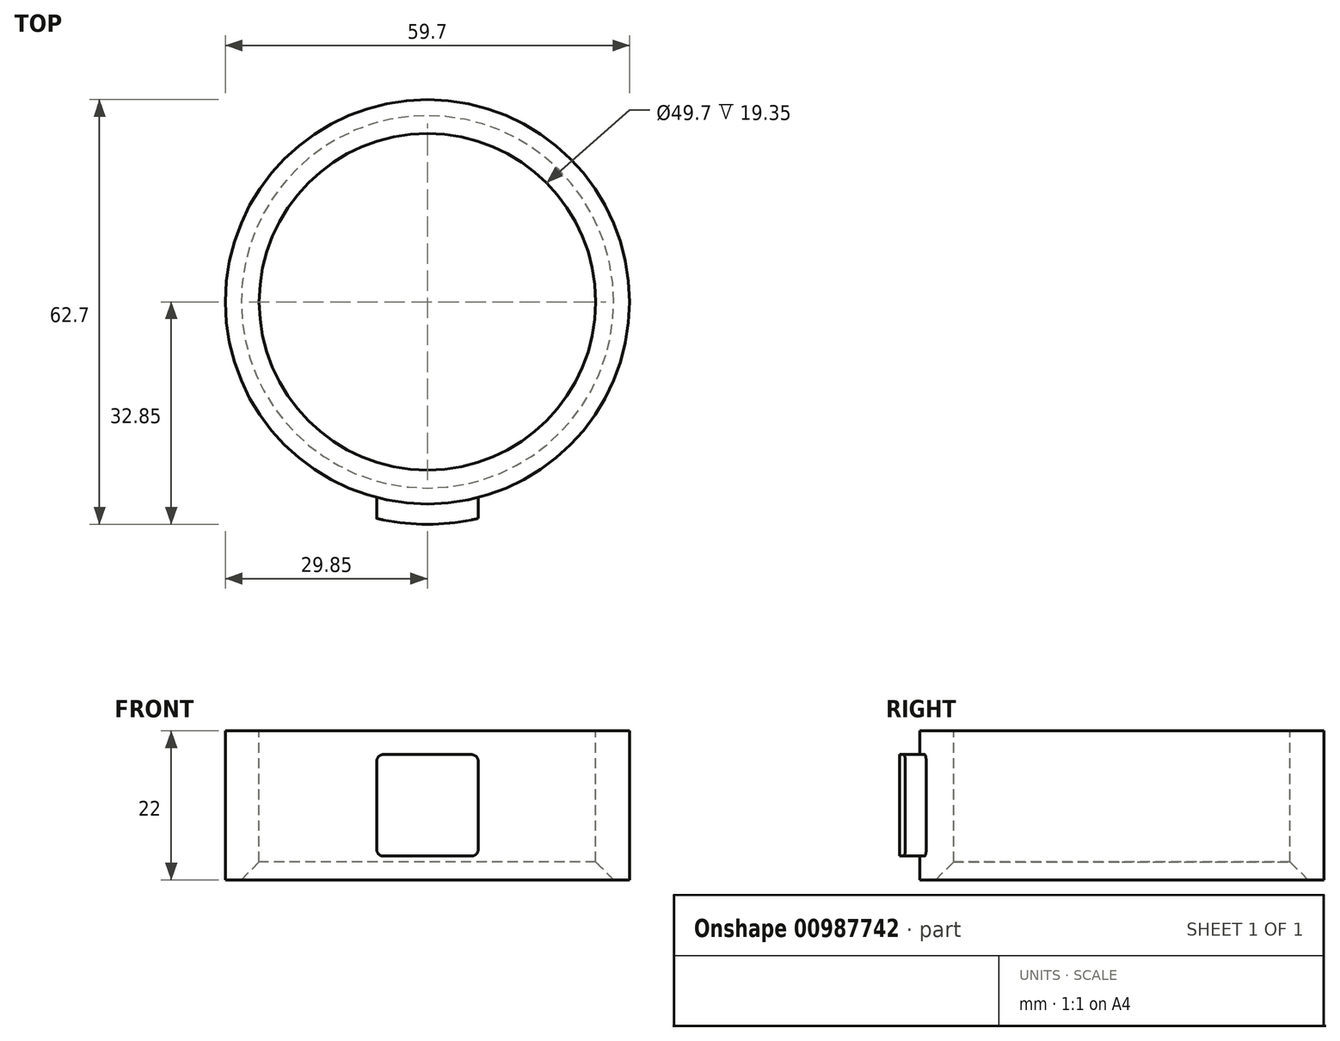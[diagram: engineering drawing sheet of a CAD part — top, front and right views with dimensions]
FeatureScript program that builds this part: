
annotation { "Feature Type Name" : "Feature", "Feature Type Description" : "" }
export const myFeature = defineFeature(function(context is Context, id is Id, definition is map)
    precondition{}
    {
        {
            var Q0;
            Q0=qCreatedBy(makeId("Front.planeOp"),FACE);
            var sketch = newSketch(context, id + "F0", { "sketchPlane" : qUnion([Q0])});
            skLineSegment(sketch, "E0", {"start": v(24.85, 0) * mm, "end": v(24.85, -19.35) * mm});
            skLineSegment(sketch, "E1", {"start": v(24.85, -19.35) * mm, "end": v(27.5, -22) * mm});
            skLineSegment(sketch, "E2", {"start": v(27.5, -22) * mm, "end": v(29.85, -22) * mm});
            skLineSegment(sketch, "E3", {"start": v(29.85, -22) * mm, "end": v(29.85, 0) * mm});
            skLineSegment(sketch, "E4", {"start": v(29.85, 0) * mm, "end": v(24.85, 0) * mm});
            skLineSegment(sketch, "E5", {"start": v(0, 0) * mm, "end": v(0, -10.6) * mm, "construction": true});
            skSolve(sketch);
        }
        {
            var Q0;
            Q0=makeQuery(id+"F0.imprint","IMPRINT",FACE,{"disambiguationData":[TD([[makeQuery(id+"F0.imprint","IMPRINT",EDGE,{"derivedFrom":sQuery(id+"F0.wireOp",EDGE,"E0")}),1.0]])]});
            var Q1;
            Q1=sQuery(id+"F0.wireOp",EDGE,"E5");
            revolve(context, id + "F1", {"surfaceOperationType" : NewSurfaceOperationType.NEW, "entities" : qUnion([Q0]), "axis" : qUnion([Q1]), "revolveType" : RevolveType.FULL});
        }
        {
            var Q0;
            Q0=qCreatedBy(makeId("Front.planeOp"),FACE);
            var sketch = newSketch(context, id + "F2", { "sketchPlane" : qUnion([Q0])});
            skLineSegment(sketch, "E6.bottom", {"start": v(-6.5, -18.5) * mm, "end": v(6.5, -18.5) * mm});
            skLineSegment(sketch, "E6.top", {"start": v(-6.5, -3.5) * mm, "end": v(6.5, -3.5) * mm});
            skLineSegment(sketch, "E6.left", {"start": v(-7.5, -17.5) * mm, "end": v(-7.5, -4.5) * mm});
            skLineSegment(sketch, "E6.right", {"start": v(7.5, -17.5) * mm, "end": v(7.5, -4.5) * mm});
            skPoint(sketch, "E7.visualSharp", {"position": v(-7.5, -3.5) * mm});
            skArc(sketch, "E7.filletArc", {"start": v(-6.5, -3.5) * mm, "mid": v(-7.2, -3.8) * mm, "end": v(-7.5, -4.5) * mm});
            skPoint(sketch, "E8.visualSharp", {"position": v(-7.5, -18.5) * mm});
            skArc(sketch, "E8.filletArc", {"start": v(-7.5, -17.5) * mm, "mid": v(-7.2, -18.2) * mm, "end": v(-6.5, -18.5) * mm});
            skPoint(sketch, "E9.visualSharp", {"position": v(7.5, -3.5) * mm});
            skArc(sketch, "E9.filletArc", {"start": v(7.5, -4.5) * mm, "mid": v(7.2, -3.8) * mm, "end": v(6.5, -3.5) * mm});
            skPoint(sketch, "E10.visualSharp", {"position": v(7.5, -18.5) * mm});
            skArc(sketch, "E10.filletArc", {"start": v(6.5, -18.5) * mm, "mid": v(7.2, -18.2) * mm, "end": v(7.5, -17.5) * mm});
            skSolve(sketch);
        }
        {
            var Q0;
            Q0 = qSketchRegion(id + "F2", true);
            extrude(context, id + "F3", {"entities" : qUnion([Q0]), "operationType" : NewBodyOperationType.ADD, "depth" : 38.3 * mm, "offsetDistance" : 25 * mm});
        }
        {
            var Q0;
            Q0=makeQuery(id+"F1.opRevolve","SWEPT_FACE",FACE,{"disambiguationData":[OSD([sQuery(id+"F0.wireOp",EDGE,"E4")])]});
            var sketch = newSketch(context, id + "F4", { "sketchPlane" : qUnion([Q0])});
            skCircle(sketch, "E11.0", {"center": v(0, 0) * mm, "radius": 24.85 * mm});
            skSolve(sketch);
        }
        {
            var Q0;
            Q0 = qSketchRegion(id + "F4", true);
            extrude(context, id + "F5", {"entities" : qUnion([Q0]), "operationType" : NewBodyOperationType.REMOVE, "oppositeDirection" : true, "depth" : 25 * mm, "offsetDistance" : 25 * mm});
        }
        {
            var Q0;
            Q0=makeQuery(id+"F1.opRevolve","SWEPT_FACE",FACE,{"disambiguationData":[OSD([sQuery(id+"F0.wireOp",EDGE,"E4")])]});
            var sketch = newSketch(context, id + "F6", { "sketchPlane" : qUnion([Q0])});
            skCircle(sketch, "E12.0", {"center": v(0, 0) * mm, "radius": 32.85 * mm});
            skCircle(sketch, "E13", {"center": v(0, 0) * mm, "radius": 51.66 * mm});
            skSolve(sketch);
        }
        {
            var Q0;
            Q0 = qSketchRegion(id + "F6", true);
            extrude(context, id + "F7", {"entities" : qUnion([Q0]), "operationType" : NewBodyOperationType.REMOVE, "oppositeDirection" : true, "depth" : 25 * mm, "offsetDistance" : 25 * mm});
        }
    });
